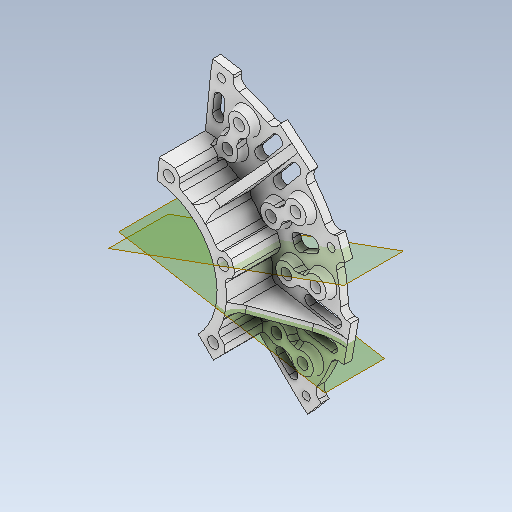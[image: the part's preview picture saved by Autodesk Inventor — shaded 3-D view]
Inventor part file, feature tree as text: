
AUTODESK INVENTOR PART (.ipt)
format: ipt  version: 2020 (Build 240168000, 168)  size: 1,392,128 bytes
history: native  units: mm
features: projected_geometry x15, chamfer x13, sketch x12, extrude x12, fillet x6, plane x4, mirror x4, thicken_offset x4, reference x4, other x3, shell x1
ambient origin geometry x8: Origin, YZ Plane, XZ Plane, XY Plane, X Axis, Y Axis, Z Axis, Center Point
bodies: Solid1 (feature_tree)
feature tree (78):
  sketch  "Sketch1"  dims[d0=50.0mm d1=57.0mm]
  plane  "Work Plane1"
  extrude  "Extrusion1"  Depth=57.0mm
  extrude  "Extrusion2"  Depth=3.0mm TaperAngle=0.0deg
  extrude  "Extrusion3"  Depth=3.0mm
  plane  "Work Plane2"
  plane  "Work Plane3"
  extrude  "Extrusion4"  Depth=3.0mm TaperAngle=0.0deg
  mirror  "Mirror1"
  extrude  "Extrusion5"  Depth=1.5mm
  extrude  "Extrusion6"  Depth=3.0mm TaperAngle=0.0deg
  extrude  "Extrusion7"  Depth=8.0mm
  extrude  "Extrusion8"  Depth=8.0mm
  extrude  "Extrusion9"  Depth=8.0mm
  thicken_offset  "Thicken1"
  thicken_offset  "Thicken2"
  thicken_offset  "Thicken3"
  thicken_offset  "Thicken4"
  extrude  "Extrusion10"  Depth=4.0mm
  mirror  "Mirror2"
  chamfer  "Chamfer1"  Distance=4.0mm
  chamfer  "Chamfer2"  Distance=3.0mm
  chamfer  "Chamfer3"  Distance=4.0mm
  chamfer  "Chamfer4"  Distance=4.0mm
  chamfer  "Chamfer5"  Distance=4.1mm
  chamfer  "Chamfer6"  Distance=4.0mm
  chamfer  "Chamfer7"  Distance=4.1mm
  chamfer  "Chamfer8"  Distance=4.0mm
  chamfer  "Chamfer9"  Distance=4.1mm
  chamfer  "Chamfer10"  Distance=7.0mm
  fillet  "Fillet1"  Radius=6.0mm
  fillet  "Fillet2"  Radius=11.0mm
  chamfer  "Chamfer11"  Distance=4.1mm
  fillet  "Fillet3"  Radius=4.1mm
  fillet  "Fillet4"  Radius=6.0mm
  fillet  "Fillet5"  Radius=11.0mm
  chamfer  "Chamfer12"  Distance=4.1mm
  fillet  "Fillet6"  Radius=4.1mm
  chamfer  "Chamfer13"  Distance=7.0mm
  extrude  "Extrusion11"  Depth=3.0mm
  plane  "Work Plane4"
  mirror  "Mirror3"
  mirror  "Mirror4"
  extrude  "Extrusion12"  Depth=3.0mm TaperAngle=360.0deg
  reference  "Reference1"
  reference  "Reference2"
  reference  "Reference3"
  sketch  "Sketch2"  dims[d2=10.0mm d3=0.0mm d4=3.0mm d5=0.0mm]
  reference  "Reference4"
  sketch  "Sketch3"  dims[d6=3.0mm d7=3.0mm]
  projected_geometry  "Projected Loop1"
  sketch  "Sketch4"  dims[d8=3.0mm d9=3.0mm d10=0.0mm]
  projected_geometry  "Projected Loop2"
  projected_geometry  "Projected Loop3"
  sketch  "Sketch5"  dims[d11=1.5mm d12=15.0mm]
  projected_geometry  "Projected Loop4"
  sketch  "Sketch6"  dims[d13=25.0mm d14=3.0mm d15=0.0mm]
  projected_geometry  "Projected Loop5"
  sketch  "Sketch7"  dims[d16=8.0mm d17=8.0mm]
  projected_geometry  "Projected Loop6"
  sketch  "Sketch8"  dims[d18=8.0mm d19=8.0mm]
  projected_geometry  "Projected Loop7"
  sketch  "Sketch9"  dims[d20=8.0mm d21=8.0mm]
  projected_geometry  "Projected Loop8"
  sketch  "Sketch10"  dims[d22=4.0mm d23=8.0mm]
  projected_geometry  "Projected Loop9"
  projected_geometry  "Projected Loop10"
  projected_geometry  "Projected Loop11"
  projected_geometry  "Projected Loop12"
  sketch  "Sketch11"  dims[d24=8.0mm]
  projected_geometry  "Projected Loop13"
  projected_geometry  "Projected Loop14"
  sketch  "Sketch12"  dims[d25=8.0mm d26=4.0mm d27=3.0mm d28=0.0mm d29=4.0mm d30=4.0mm d31=4.1mm d32=4.0mm d33=4.1mm d34=4.0mm d35=4.1mm d36=7.0mm d37=0.0mm d38=6.0mm d39=11.0mm d40=4.1mm d41=4.1mm d42=6.0mm d43=11.0mm d44=4.1mm d45=4.1mm d46=7.0mm d47=0.0mm d48=4.2mm d49=60.0mm d51=360.0deg d53=4.2mm d54=60.0mm d56=360.0deg d58=4.2mm d59=60.0mm d61=360.0deg d63=4.2mm d64=60.0mm d66=360.0deg d68=2.0mm d69=0.0mm d70=10.0mm d71=10.0mm d72=10.0mm d73=10.0mm d74=3.0mm d75=0.0mm d76=1.0mm d77=1.0mm d78=1.0mm d79=1.0mm d80=1.0mm d81=1.0mm d82=1.0mm d83=1.0mm d84=3.0mm d85=0.0mm d86=1.0mm d87=3.0mm d88=45.0deg d89=1.0mm d90=3.0mm d91=45.0deg d92=1.0mm d93=3.0mm d94=45.0deg d95=1.0mm d96=3.0mm d97=45.0deg d98=1.0mm d99=3.0mm d100=45.0deg d101=1.0mm d102=3.0mm d103=45.0deg d104=1.0mm d105=3.0mm d106=45.0deg d107=1.0mm d108=3.0mm d109=45.0deg d110=1.0mm d111=3.0mm d112=45.0deg d113=1.0mm d114=3.0mm d115=45.0deg d116=2.0mm d117=2.0mm d118=2.0mm d119=3.0mm d120=45.0deg d121=2.0mm d122=6.0mm d123=20.0mm d124=2.0mm d125=3.0mm d126=45.0deg d127=2.0mm d128=2.0mm d129=3.0mm d130=45.0deg d131=10.0mm d132=3.0mm d133=5.0mm d134=4.0mm d135=4.0mm d136=3.0mm d137=4.0mm d138=3.0mm d139=0.0mm d140=3.0mm d141=0.0mm]
  projected_geometry  "Projected Loop15"
  parser-record x1  (decoder bookkeeping rows leaked as tree rows — omitted from the tree; the rows remain in map.json)
  other  "reducer_2.iam"
  other  "xl_20:1"
  shell  "shell_3:1"  Thickness=4.2mm
note: 1 file-system path scrubbed to <path> (originals preserved in map.json)
